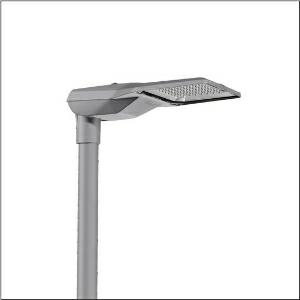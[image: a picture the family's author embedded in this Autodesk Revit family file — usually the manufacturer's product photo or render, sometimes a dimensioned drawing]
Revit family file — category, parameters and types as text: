
# Revit family: streetlight_sl_21_midi___p0_8a_5xe3u33s08mb_2792
name_source: partatom
category: Lighting Fixtures
units: mm (PartAtom-declared; Revit-internal decimal feet)

## family parameters
Cut with Voids When Loaded = No
Host = Face
Light Source = No
Part Type = Normal
Room Calculation Point = No
Round Connector Dimension = Use Diameter
Shared = No

## types (1)
- --- (1 x LED, 18430 lm, 136 W, 3000K)
    Apparent Load = 136 VA
    CIE Flux Codes = 33 69 96 100 100
    Color Rendering = 70
    Color Temperature = 3000K
    Default Elevation = 1800 mm
    Description = Streetlight SL 21 midi, mast luminaire, primary light control with lens, of PMMA, primary optical cover: cover, of toughened safety glass, transparent, light distribution: P0.8a, light emission: direct distribution, primary light characteristic: asymmetric, installation type: post-top, side-entry, LED, High Power LED, rated luminous flux: 18.430lm, luminous efficacy: 136lm/W, light colour: 730, colour temperature: 3000K, control gear: D4i, control: pre-setting: logarithmic dimming characteristic, flexible luminous flux parameterisation, time-dependent luminous flux control, constant luminous flux control, overheat protection, mains connection: 230..240V, AC, 50/60Hz, start of lifetime: 136W, end of service life: 142W, reduction: 61W, luminaire housing, of diecast aluminium, powder-coated, SITECO metallic grey (DB 702S), corrosivity category C5 high according to DIN EN ISO 12944, multi-level sealing system, sealing non-destructively replaceable, inclination adjustable: 0°, 5°, 10°, 15°, please order mast flange separately, length: 644mm, width: 335mm, height: 110mm, mast flange for spigot size: 42mm (side-entry): 5XC10008XM4, 60/48mm (side-entry/post-top): 5XC10108XM2, 76/60mm (side-entry/post-top): 5XC10108XM1, mounting height: 4..8m, Smart Interface above, protection rating (complete): IP66, insulation class (complete): insulation class II (safety insulation), certification: CE, ENEC, ENEC+, VDE, impact resistance: IK10, permissible operating ambient temperature for outdoor applications: -40..+50°C, standard-compliant lighting for roads and squares, packaging unit: 1 piece

Light Distribution: P0.8a
    Height = 111 mm
    Lamp = 1 x LED
    Lamp Light Flux = 18430 lm
    Lamp Power = 136 W
    Lamp count = 1
    Length = 644 mm
    Luminous efficacy = 136 lm/W
    Manufacturer = Siteco
    ModVariant = No
    Model = 5XE3U33S08MB
    Number of Poles = 1
    OnlyDefault = Yes
    Power Factor = 1
    Product Name = Streetlight SL 21 midi | P0.8a
    Product group = mast luminaire | pylon top
    ProductGroupID = 6100
    Protection Class = Protection class II
    Protection Degree = IP 66
    RLX_Detail_Level = 1
    RLX_Emergency_Light_Flux = 0 lm
    RLX_Emergency_Type = 0
    RLX_Emergency_Type_DB = No
    RlxData = <blob elided: 90661 chars, md5=7689536c>
    Socket = socket
    Standby Power = 0 W
    System Light Flux = 18429 lm
    System Power = 136 W
    Type Comments = factory setting: luminous flux: 100 % | dim-lin: 254 | 695 mA
    Type Image = l_1004302.jpg
    URL = http://relux.com
    VarID = @adj_080365
    Voltage = 0 V
    Weight = 0.00 kg
    Width = 336 mm

## geometry (parser evidence)
native form markers: Blend x4, Sweep x12
no freeform markers — native parametric forms only
